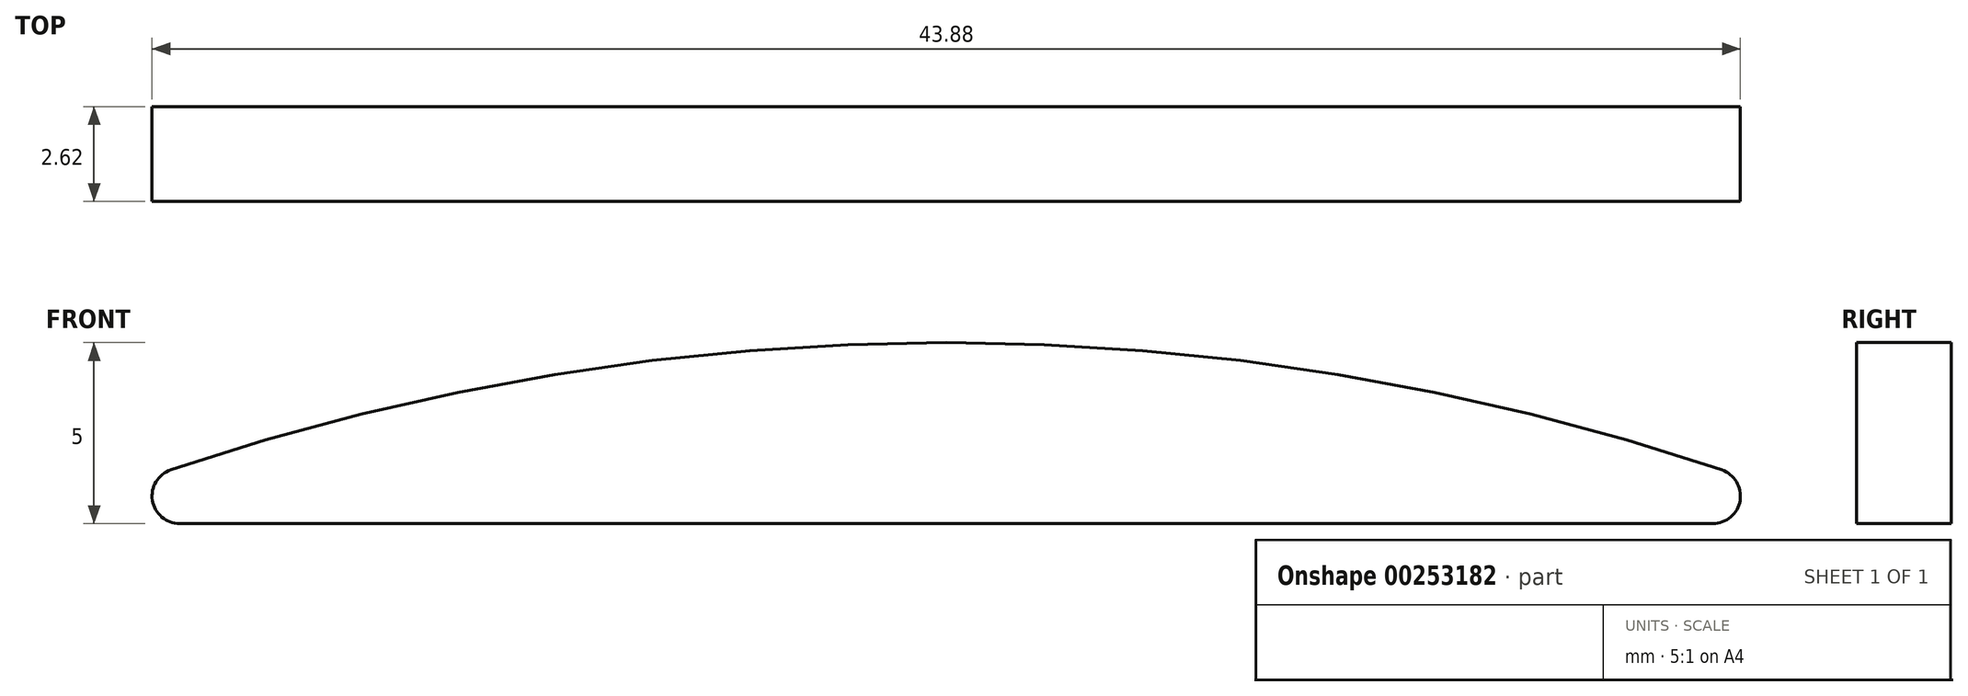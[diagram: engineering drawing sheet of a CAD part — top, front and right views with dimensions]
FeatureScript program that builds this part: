
annotation { "Feature Type Name" : "Feature", "Feature Type Description" : "" }
export const myFeature = defineFeature(function(context is Context, id is Id, definition is map)
    precondition{}
    {
        {
            var Q0;
            Q0=qCreatedBy(makeId("Front.planeOp"),FACE);
            var sketch = newSketch(context, id + "F0", { "sketchPlane" : qUnion([Q0])});
            skLineSegment(sketch, "E0", {"start": v(25.4, 25.4) * mm, "end": v(-25.4, 25.4) * mm});
            skLineSegment(sketch, "E1", {"start": v(0, 25.4) * mm, "end": v(0, 20.4) * mm});
            skArc(sketch, "E2", {"start": v(-25.4, 25.4) * mm, "mid": v(0, 20.4) * mm, "end": v(25.4, 25.4) * mm});
            skLineSegment(sketch, "E3", {"start": v(25.4, 25.4) * mm, "end": v(25.4, -25.4) * mm});
            skLineSegment(sketch, "E4", {"start": v(25.4, 0) * mm, "end": v(20.4, 0) * mm});
            skArc(sketch, "E5", {"start": v(25.4, 25.4) * mm, "mid": v(20.4, 0) * mm, "end": v(25.4, -25.4) * mm});
            skArc(sketch, "E6.MirrorCS", {"start": v(-25.4, -25.4) * mm, "mid": v(0, -20.4) * mm, "end": v(25.4, -25.4) * mm});
            skLineSegment(sketch, "E7.MirrorCS", {"start": v(25.4, -25.4) * mm, "end": v(-25.4, -25.4) * mm});
            skLineSegment(sketch, "E8.MirrorCS", {"start": v(-25.4, 25.4) * mm, "end": v(-25.4, -25.4) * mm});
            skArc(sketch, "E9.MirrorCS", {"start": v(-25.4, 25.4) * mm, "mid": v(-20.4, 0) * mm, "end": v(-25.4, -25.4) * mm});
            skSolve(sketch);
        }
        {
            var Q0;
            {var subQ1=sQuery(id+"F0.wireOp",EDGE,"E6.MirrorCS");Q0=makeQuery(id+"F0.imprint","IMPRINT",FACE,{"disambiguationData":[TD([[makeQuery(id+"F0.imprint","IMPRINT",EDGE,{"derivedFrom":subQ1}),1.0]])]});}
            extrude(context, id + "F1", {"entities" : qUnion([Q0]), "depth" : 2.62 * mm});
        }
        {
            var Q0;
            Q0=makeQuery(id+"F1.opExtrude","CAP_FACE",FACE,{"disambiguationData":[OSD([sQuery(id+"F0.wireOp",EDGE,"E2"),sQuery(id+"F0.wireOp",EDGE,"E5"),sQuery(id+"F0.wireOp",EDGE,"E6.MirrorCS"),sQuery(id+"F0.wireOp",EDGE,"E9.MirrorCS")])],"isStart":true});
            var sketch = newSketch(context, id + "F2", { "sketchPlane" : qUnion([Q0])});
            skLineSegment(sketch, "E10.rect.bottom", {"start": v(-4.89, -4.89) * mm, "end": v(4.89, -4.89) * mm});
            skLineSegment(sketch, "E10.rect.top", {"start": v(-4.89, 4.89) * mm, "end": v(4.89, 4.89) * mm});
            skLineSegment(sketch, "E10.rect.left", {"start": v(-4.89, -4.89) * mm, "end": v(-4.89, 4.89) * mm});
            skLineSegment(sketch, "E10.rect.right", {"start": v(4.89, -4.89) * mm, "end": v(4.89, 4.89) * mm});
            skPoint(sketch, "E10.rect.middle", {"position": v(0, 0) * mm});
            skSolve(sketch);
        }
        {
            var Q0;
            Q0=makeQuery(id+"F2.imprint","IMPRINT",FACE,{"disambiguationData":[TD([[makeQuery(id+"F2.imprint","IMPRINT",EDGE,{"derivedFrom":sQuery(id+"F2.wireOp",EDGE,"E10.rect.bottom")}),1.0]])]});
            extrude(context, id + "F3", {"entities" : qUnion([Q0]), "operationType" : NewBodyOperationType.REMOVE, "oppositeDirection" : true, "depth" : 25 * mm});
        }
        {
            var Q0;
            Q0=makeQuery(id+"F1.opExtrude","SWEPT_EDGE",EDGE,{"disambiguationData":[OSD([sQuery(id+"F0.wireOp",EDGE,"E0"),sQuery(id+"F0.wireOp",EDGE,"E2"),sQuery(id+"F0.wireOp",EDGE,"E3"),sQuery(id+"F0.wireOp",EDGE,"E5")])]});
            var Q1;
            Q1=makeQuery(id+"F1.opExtrude","SWEPT_EDGE",EDGE,{"disambiguationData":[OSD([sQuery(id+"F0.wireOp",EDGE,"E0"),sQuery(id+"F0.wireOp",EDGE,"E2"),sQuery(id+"F0.wireOp",EDGE,"E8.MirrorCS"),sQuery(id+"F0.wireOp",EDGE,"E9.MirrorCS")])]});
            var Q2;
            Q2=makeQuery(id+"F1.opExtrude","SWEPT_EDGE",EDGE,{"disambiguationData":[OSD([sQuery(id+"F0.wireOp",EDGE,"E6.MirrorCS"),sQuery(id+"F0.wireOp",EDGE,"E7.MirrorCS"),sQuery(id+"F0.wireOp",EDGE,"E8.MirrorCS"),sQuery(id+"F0.wireOp",EDGE,"E9.MirrorCS")])]});
            var Q3;
            Q3=makeQuery(id+"F1.opExtrude","SWEPT_EDGE",EDGE,{"disambiguationData":[OSD([sQuery(id+"F0.wireOp",EDGE,"E3"),sQuery(id+"F0.wireOp",EDGE,"E5"),sQuery(id+"F0.wireOp",EDGE,"E6.MirrorCS"),sQuery(id+"F0.wireOp",EDGE,"E7.MirrorCS")])]});
            fillet(context, id + "F4", {"entities" : qUnion([Q0, Q1, Q2, Q3]), "radius" : 0.76 * mm, "tangentPropagation" : true, "allowEdgeOverflow" : false});
        }
    });
